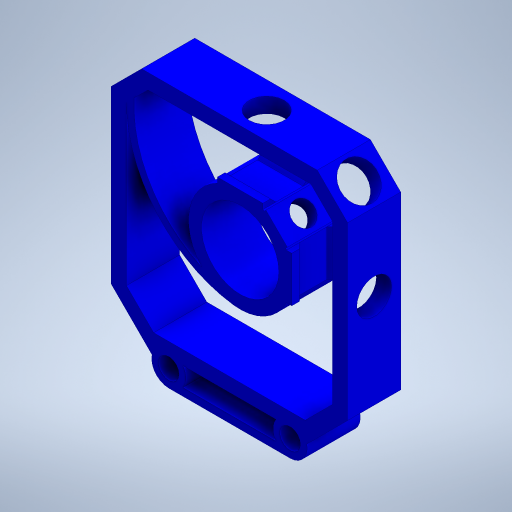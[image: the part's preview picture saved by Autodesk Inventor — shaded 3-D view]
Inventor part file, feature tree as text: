
AUTODESK INVENTOR PART (.ipt)
format: ipt  version: 2023.1 (Build 271208000, 208)  size: 485,376 bytes
history: native  units: mm
features: extrude x6, sketch x5, projected_geometry x4, reference x3, other x2, plane x1, mirror x1, pattern_linear x1
ambient origin geometry x8: Origin, YZ Plane, XZ Plane, XY Plane, X Axis, Y Axis, Z Axis, Center Point
bodies: Solid1 (feature_tree)
feature tree (23):
  extrude  "Extrusion1"  Depth=1.25mm
  extrude  "Extrusion2"  TaperAngle=45.0deg  [1 undecoded]
  extrude  "Extrusion3"  Depth=0.675mm
  extrude  "Extrusion4"  Depth=0.625mm
  plane  "Work Plane1"
  mirror  "Mirror1"
  sketch  "Sketch5"  dims[d8=7.5mm d9=1.25mm d10=0.625mm d11=5.0mm d12=135.0deg d13=1.25mm d14=2.0mm d15=2.0mm d16=38.935534mm d17=38.935534mm d18=9.25mm d19=9.25mm d20=9.25mm d21=9.25mm d22=5.0mm d23=5.0mm d24=5.0mm d25=5.0mm d26=2.5mm d28=8.75mm d29=0.0mm d30=0.875mm d31=8.75mm d32=0.0mm d33=5.75mm d34=10.0mm d35=0.0mm d36=1.25mm d37=135.0deg d38=10.0mm d39=0.0mm d40=3.75mm d41=6.0mm d42=5.0mm d43=0.0mm d44=10.0mm d45=0.0mm d46=2.5mm d47=1.25mm d48=20.0mm d50=8.75mm d51=0.1425mm d52=0.1445mm]
  extrude  "Extrusion5"  Depth=10.0mm
  extrude  "Extrusion6"  Depth=10.0mm
  pattern_linear  "Rectangular Pattern1"  Spacing1=5.0mm  [1 undecoded]
  sketch  "Sketch1"  dims[d0=1.25mm d1=1.25mm]
  reference  "Reference1"
  reference  "Reference2"
  reference  "Reference3"
  sketch  "Sketch2"  dims[d2=2.5mm d3=45.0deg]
  sketch  "Sketch3"  dims[d4=12.75mm d5=0.675mm]
  projected_geometry  "Projected Loop1"
  sketch  "Sketch4"  dims[d6=2.125mm d7=0.625mm]
  projected_geometry  "Projected Loop2"
  projected_geometry  "Projected Loop5"
  projected_geometry  "Projected Loop6"
  other  "Cube 1x1 V5.iam"
  other  "Cube 1x1 Bottom V5:1"
note: 2 required parameter values undecoded (feature->parameter linkage not recoverable at this tier; creation-order binding heuristic only, values carry confidence <= 0.55)
